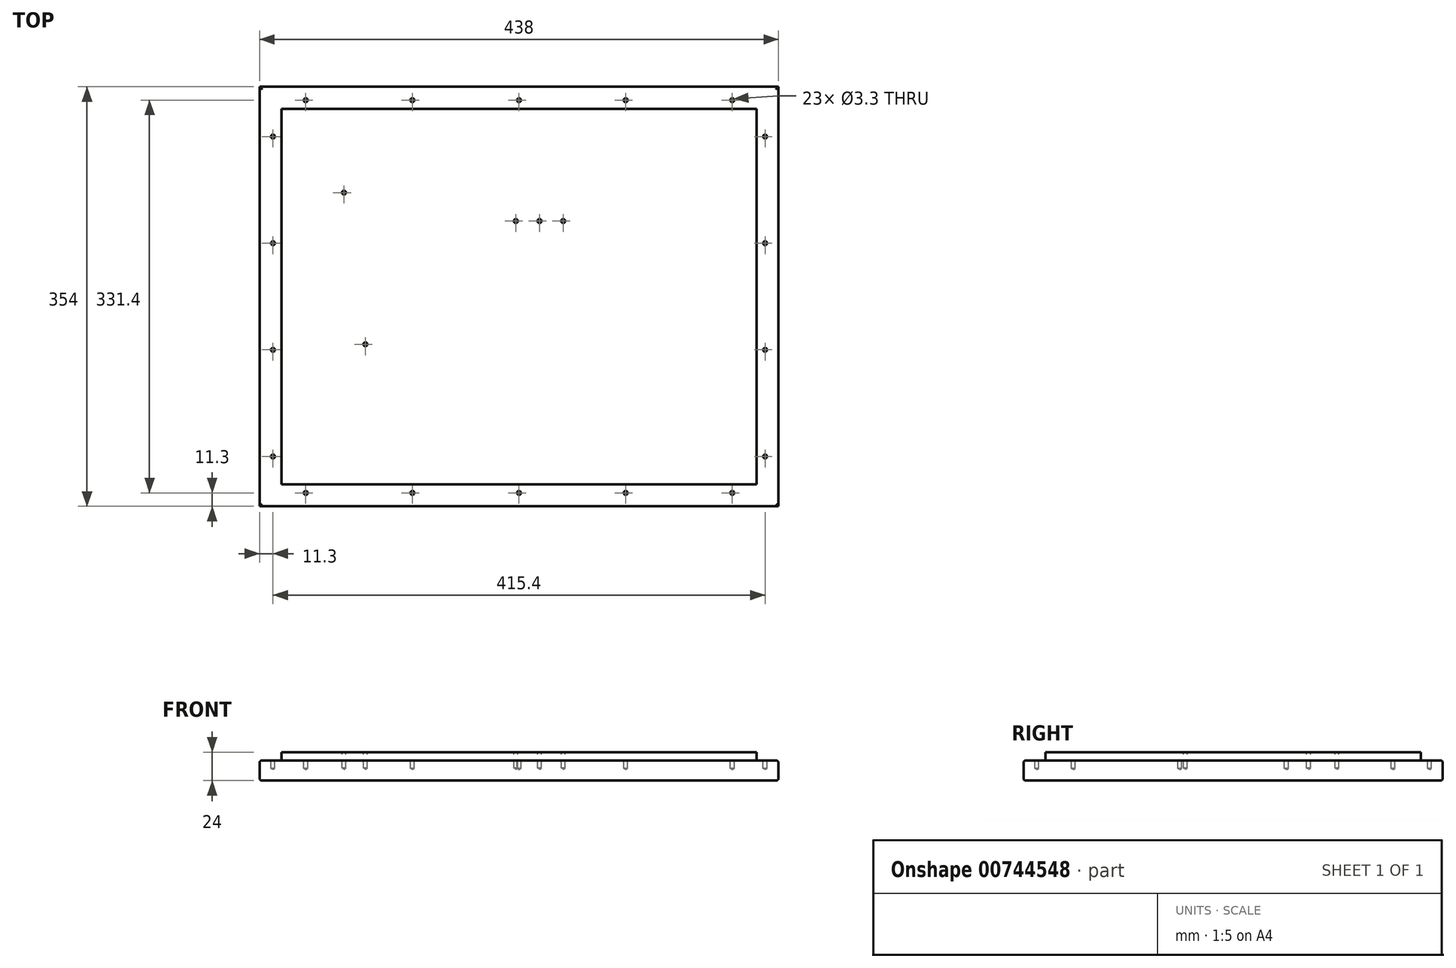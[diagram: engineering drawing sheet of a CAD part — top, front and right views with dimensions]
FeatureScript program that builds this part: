
annotation { "Feature Type Name" : "Feature", "Feature Type Description" : "" }
export const myFeature = defineFeature(function(context is Context, id is Id, definition is map)
    precondition{}
    {
        {
            var Q0;
            Q0=qCreatedBy(makeId("Top.planeOp"),FACE);
            var sketch = newSketch(context, id + "F0", { "sketchPlane" : qUnion([Q0])});
            skLineSegment(sketch, "E0.bottom", {"start": v(0, 0) * mm, "end": v(438, 0) * mm});
            skLineSegment(sketch, "E0.top", {"start": v(0, 354) * mm, "end": v(438, 354) * mm});
            skLineSegment(sketch, "E0.left", {"start": v(0, 0) * mm, "end": v(0, 354) * mm});
            skLineSegment(sketch, "E0.right", {"start": v(438, 0) * mm, "end": v(438, 354) * mm});
            skLineSegment(sketch, "E1.bottom", {"start": v(18.5, 18.5) * mm, "end": v(419.5, 18.5) * mm});
            skLineSegment(sketch, "E1.top", {"start": v(18.5, 335.5) * mm, "end": v(419.5, 335.5) * mm});
            skLineSegment(sketch, "E1.left", {"start": v(18.5, 18.5) * mm, "end": v(18.5, 335.5) * mm});
            skLineSegment(sketch, "E1.right", {"start": v(419.5, 18.5) * mm, "end": v(419.5, 335.5) * mm});
            skSolve(sketch);
        }
        {
            var Q0;
            Q0 = qSketchRegion(id + "F0", true);
            extrude(context, id + "F1", {"entities" : qUnion([Q0]), "depth" : 17 * mm, "offsetDistance" : 25 * mm});
        }
        {
            var Q0;
            Q0=makeQuery(id+"F0.imprint","IMPRINT",FACE,{"disambiguationData":[TD([[makeQuery(id+"F0.imprint","IMPRINT",EDGE,{"derivedFrom":sQuery(id+"F0.wireOp",EDGE,"E1.bottom")}),1.0]])]});
            extrude(context, id + "F2", {"entities" : qUnion([Q0]), "operationType" : NewBodyOperationType.ADD, "depth" : 24 * mm, "offsetDistance" : 25 * mm});
        }
        {
            var Q0;
            {var subQ0=sQuery(id+"F0.wireOp",EDGE,"E1.right");var subQ1=sQuery(id+"F0.wireOp",EDGE,"E1.left");var subQ2=sQuery(id+"F0.wireOp",EDGE,"E1.top");var subQ3=sQuery(id+"F0.wireOp",EDGE,"E1.bottom");Q0=makeQuery(id+"F2.boolean.opBoolean","MERGE",FACE,{"derivedFrom":[makeQuery(id+"F1.opExtrude","CAP_FACE",FACE,{"disambiguationData":[OSD([sQuery(id+"F0.wireOp",EDGE,"E0.bottom"),sQuery(id+"F0.wireOp",EDGE,"E0.top"),sQuery(id+"F0.wireOp",EDGE,"E0.left"),sQuery(id+"F0.wireOp",EDGE,"E0.right"),subQ3,subQ2,subQ1,subQ0])],"isStart":true}),makeQuery(id+"F2.opExtrude","CAP_FACE",FACE,{"disambiguationData":[OSD([subQ3,subQ2,subQ1,subQ0])],"isStart":true})]});}
            fillet(context, id + "F3", {"entities" : qUnion([Q0]), "radius" : 2 * mm, "tangentPropagation" : true, "allowEdgeOverflow" : false});
        }
        {
            var Q0;
            Q0=makeQuery(id+"F1.opExtrude","CAP_EDGE",EDGE,{"disambiguationData":[OSD([sQuery(id+"F0.wireOp",EDGE,"E0.right")])],"isStart":false});
            var Q1;
            Q1=makeQuery(id+"F1.opExtrude","CAP_EDGE",EDGE,{"disambiguationData":[OSD([sQuery(id+"F0.wireOp",EDGE,"E0.bottom")])],"isStart":false});
            var Q2;
            Q2=makeQuery(id+"F1.opExtrude","CAP_EDGE",EDGE,{"disambiguationData":[OSD([sQuery(id+"F0.wireOp",EDGE,"E0.top")])],"isStart":false});
            var Q3;
            Q3=makeQuery(id+"F1.opExtrude","CAP_EDGE",EDGE,{"disambiguationData":[OSD([sQuery(id+"F0.wireOp",EDGE,"E0.left")])],"isStart":false});
            fillet(context, id + "F4", {"entities" : qUnion([Q0, Q1, Q2, Q3]), "radius" : 2 * mm, "tangentPropagation" : true, "allowEdgeOverflow" : false});
        }
        {
            var Q0;
            Q0=makeQuery(id+"F1.opExtrude","CAP_FACE",FACE,{"disambiguationData":[OSD([sQuery(id+"F0.wireOp",EDGE,"E0.bottom"),sQuery(id+"F0.wireOp",EDGE,"E0.top"),sQuery(id+"F0.wireOp",EDGE,"E0.left"),sQuery(id+"F0.wireOp",EDGE,"E0.right"),sQuery(id+"F0.wireOp",EDGE,"E1.bottom"),sQuery(id+"F0.wireOp",EDGE,"E1.top"),sQuery(id+"F0.wireOp",EDGE,"E1.left"),sQuery(id+"F0.wireOp",EDGE,"E1.right")])],"isStart":false});
            var sketch = newSketch(context, id + "F5", { "sketchPlane" : qUnion([Q0])});
            skLineSegment(sketch, "E2", {"start": v(-30.1, 0) * mm, "end": v(521.52, 0) * mm, "construction": true});
            skLineSegment(sketch, "E3", {"start": v(-30.1, 42) * mm, "end": v(521.52, 42) * mm, "construction": true});
            skLineSegment(sketch, "E4", {"start": v(-30.1, 132) * mm, "end": v(521.52, 132) * mm, "construction": true});
            skLineSegment(sketch, "E5", {"start": v(-30.1, 222) * mm, "end": v(521.52, 222) * mm, "construction": true});
            skLineSegment(sketch, "E6", {"start": v(-30.1, 312) * mm, "end": v(521.52, 312) * mm, "construction": true});
            skLineSegment(sketch, "E7", {"start": v(0, -86.71) * mm, "end": v(0, 453.17) * mm, "construction": true});
            skLineSegment(sketch, "E8", {"start": v(11.3, -86.71) * mm, "end": v(11.3, 453.17) * mm, "construction": true});
            skLineSegment(sketch, "E9", {"start": v(426.7, -86.71) * mm, "end": v(426.7, 453.17) * mm, "construction": true});
            skLineSegment(sketch, "E10", {"start": v(0, 11.3) * mm, "end": v(551.61, 11.3) * mm, "construction": true});
            skLineSegment(sketch, "E11", {"start": v(0, 342.7) * mm, "end": v(482.91, 342.7) * mm, "construction": true});
            skLineSegment(sketch, "E12", {"start": v(39, -170.33) * mm, "end": v(39, 686.71) * mm, "construction": true});
            skLineSegment(sketch, "E13", {"start": v(129, -173.4) * mm, "end": v(129, 659.37) * mm, "construction": true});
            skLineSegment(sketch, "E14", {"start": v(219, -168.8) * mm, "end": v(219, 663.2) * mm, "construction": true});
            skLineSegment(sketch, "E15", {"start": v(309, -131.93) * mm, "end": v(309, 662.44) * mm, "construction": true});
            skLineSegment(sketch, "E16", {"start": v(399, -90.46) * mm, "end": v(399, 665.5) * mm, "construction": true});
            skPoint(sketch, "E17", {"position": v(219, 18.5) * mm});
            skCircle(sketch, "E18", {"center": v(11.3, 312) * mm, "radius": 2 * mm});
            skCircle(sketch, "E19", {"center": v(11.3, 222) * mm, "radius": 2 * mm});
            skCircle(sketch, "E20", {"center": v(11.3, 132) * mm, "radius": 2 * mm});
            skCircle(sketch, "E21", {"center": v(11.3, 42) * mm, "radius": 2 * mm});
            skCircle(sketch, "E22", {"center": v(426.7, 312) * mm, "radius": 2 * mm});
            skCircle(sketch, "E23", {"center": v(426.7, 222) * mm, "radius": 2 * mm});
            skCircle(sketch, "E24", {"center": v(426.7, 132) * mm, "radius": 2 * mm});
            skCircle(sketch, "E25", {"center": v(426.7, 42) * mm, "radius": 2 * mm});
            skCircle(sketch, "E26", {"center": v(39, 11.3) * mm, "radius": 2 * mm});
            skCircle(sketch, "E27", {"center": v(129, 11.3) * mm, "radius": 2 * mm});
            skCircle(sketch, "E28", {"center": v(219, 11.3) * mm, "radius": 2 * mm});
            skCircle(sketch, "E29", {"center": v(309, 11.3) * mm, "radius": 2 * mm});
            skCircle(sketch, "E30", {"center": v(399, 11.3) * mm, "radius": 2 * mm});
            skCircle(sketch, "E31", {"center": v(399, 342.7) * mm, "radius": 2 * mm});
            skCircle(sketch, "E32", {"center": v(309, 342.7) * mm, "radius": 2 * mm});
            skCircle(sketch, "E33", {"center": v(219, 342.7) * mm, "radius": 2 * mm});
            skCircle(sketch, "E34", {"center": v(129, 342.7) * mm, "radius": 2 * mm});
            skCircle(sketch, "E35", {"center": v(39, 342.7) * mm, "radius": 2 * mm});
            skSolve(sketch);
        }
        {
            var Q0;
            Q0=sQuery(id+"F5.wireOp",VERTEX,"E18.center");
            var Q1;
            Q1=sQuery(id+"F5.wireOp",VERTEX,"E19.center");
            var Q2;
            Q2=sQuery(id+"F5.wireOp",VERTEX,"E20.center");
            var Q3;
            Q3=sQuery(id+"F5.wireOp",VERTEX,"E21.center");
            var Q4;
            Q4=sQuery(id+"F5.wireOp",VERTEX,"E26.center");
            var Q5;
            Q5=sQuery(id+"F5.wireOp",VERTEX,"E27.center");
            var Q6;
            Q6=sQuery(id+"F5.wireOp",VERTEX,"E28.center");
            var Q7;
            Q7=sQuery(id+"F5.wireOp",VERTEX,"E29.center");
            var Q8;
            Q8=sQuery(id+"F5.wireOp",VERTEX,"E30.center");
            var Q9;
            Q9=sQuery(id+"F5.wireOp",VERTEX,"E25.center");
            var Q10;
            Q10=sQuery(id+"F5.wireOp",VERTEX,"E24.center");
            var Q11;
            Q11=sQuery(id+"F5.wireOp",VERTEX,"E23.center");
            var Q12;
            Q12=sQuery(id+"F5.wireOp",VERTEX,"E22.center");
            var Q13;
            Q13=sQuery(id+"F5.wireOp",VERTEX,"E31.center");
            var Q14;
            Q14=sQuery(id+"F5.wireOp",VERTEX,"E32.center");
            var Q15;
            Q15=sQuery(id+"F5.wireOp",VERTEX,"E33.center");
            var Q16;
            Q16=sQuery(id+"F5.wireOp",VERTEX,"E34.center");
            var Q17;
            Q17=sQuery(id+"F5.wireOp",VERTEX,"E35.center");
            var Q18;
            Q18=makeQuery(id+"F1.opExtrude","SWEPT_BODY",BODY,{"disambiguationData":[OSD([sQuery(id+"F0.wireOp",EDGE,"E0.bottom"),sQuery(id+"F0.wireOp",EDGE,"E0.top"),sQuery(id+"F0.wireOp",EDGE,"E0.left"),sQuery(id+"F0.wireOp",EDGE,"E0.right"),sQuery(id+"F0.wireOp",EDGE,"E1.bottom"),sQuery(id+"F0.wireOp",EDGE,"E1.top"),sQuery(id+"F0.wireOp",EDGE,"E1.left"),sQuery(id+"F0.wireOp",EDGE,"E1.right")])]});
            hole(context, id + "F6", {"style" : HoleStyle.SIMPLE, "endStyle" : HoleEndStyle.BLIND, "standardTappedOrClearance" : lookupTablePath({ "standard" : "ISO", "engagement" : "75%", "pitch" : "0.7 mm", "size" : "M4", "type" : "Tapped" }), "standardBlindInLast" : lookupTablePath({ "standard" : "ISO", "engagement" : "75%", "pitch" : "0.7 mm", "size" : "M4", "type" : "Tapped" }), "holeDiameter" : 3.3 * mm, "majorDiameter" : 4 * mm, "showTappedDepth" : true, "holeDepth" : 6.6 * mm, "isTappedThrough" : true, "tappedDepth" : 5.9 * mm, "tapClearance" : 1, "locations" : qUnion([Q0, Q1, Q2, Q3, Q4, Q5, Q6, Q7, Q8, Q9, Q10, Q11, Q12, Q13, Q14, Q15, Q16, Q17]), "scope" : qUnion([Q18])});
        }
        {
            var Q0;
            Q0=makeQuery(id+"F2.opExtrude","CAP_FACE",FACE,{"disambiguationData":[OSD([sQuery(id+"F0.wireOp",EDGE,"E1.bottom"),sQuery(id+"F0.wireOp",EDGE,"E1.top"),sQuery(id+"F0.wireOp",EDGE,"E1.left"),sQuery(id+"F0.wireOp",EDGE,"E1.right")])],"isStart":false});
            var sketch = newSketch(context, id + "F7", { "sketchPlane" : qUnion([Q0])});
            skCircle(sketch, "E36", {"center": v(216.3, 240.7) * mm, "radius": 1.5 * mm});
            skCircle(sketch, "E37.0", {"center": v(11.3, 222) * mm, "radius": 1.65 * mm});
            skCircle(sketch, "E38.0", {"center": v(219, 342.7) * mm, "radius": 1.65 * mm});
            skCircle(sketch, "E39.0", {"center": v(11.3, 312) * mm, "radius": 1.65 * mm});
            skCircle(sketch, "E40.0", {"center": v(39, 342.7) * mm, "radius": 1.65 * mm});
            skCircle(sketch, "E41.1.0.0", {"center": v(236.3, 240.7) * mm, "radius": 1.5 * mm});
            skCircle(sketch, "E41.2.0.0", {"center": v(256.3, 240.7) * mm, "radius": 1.5 * mm});
            skLineSegment(sketch, "E41.direction1", {"start": v(216.3, 240.7) * mm, "end": v(236.3, 240.7) * mm, "construction": true});
            skCircle(sketch, "E42", {"center": v(71.3, 264.7) * mm, "radius": 1.5 * mm});
            skCircle(sketch, "E43", {"center": v(89.3, 136.7) * mm, "radius": 1.5 * mm});
            skLineSegment(sketch, "E44", {"start": v(104.3, 335.5) * mm, "end": v(104.3, 18.5) * mm, "construction": true});
            skSolve(sketch);
        }
        {
            var Q0;
            Q0=sQuery(id+"F7.wireOp",VERTEX,"E41.direction1.start");
            var Q1;
            Q1=sQuery(id+"F7.wireOp",VERTEX,"E41.direction1.end");
            var Q2;
            Q2=sQuery(id+"F7.wireOp",VERTEX,"E41.2.0.0.center");
            var Q3;
            Q3=makeQuery(id+"F1.opExtrude","SWEPT_BODY",BODY,{"disambiguationData":[OSD([sQuery(id+"F0.wireOp",EDGE,"E0.bottom"),sQuery(id+"F0.wireOp",EDGE,"E0.top"),sQuery(id+"F0.wireOp",EDGE,"E0.left"),sQuery(id+"F0.wireOp",EDGE,"E0.right"),sQuery(id+"F0.wireOp",EDGE,"E1.bottom"),sQuery(id+"F0.wireOp",EDGE,"E1.top"),sQuery(id+"F0.wireOp",EDGE,"E1.left"),sQuery(id+"F0.wireOp",EDGE,"E1.right")])]});
            hole(context, id + "F8", {"style" : HoleStyle.SIMPLE, "endStyle" : HoleEndStyle.BLIND, "standardTappedOrClearance" : lookupTablePath({ "fit" : "Normal", "standard" : "ISO", "size" : "M3", "type" : "Clearance" }), "standardBlindInLast" : lookupTablePath({ "fit" : "Standard", "standard" : "ISO", "size" : "M3", "type" : "Clearance" }), "holeDiameter" : 3.3 * mm, "majorDiameter" : 3 * mm, "holeDepth" : 13.5 * mm, "isTappedThrough" : true, "tappedDepth" : 12 * mm, "tapClearance" : 3, "locations" : qUnion([Q0, Q1, Q2]), "scope" : qUnion([Q3])});
        }
        {
            var Q0;
            Q0=sQuery(id+"F7.wireOp",VERTEX,"E42.center");
            var Q1;
            Q1=sQuery(id+"F7.wireOp",VERTEX,"E43.center");
            var Q2;
            Q2=makeQuery(id+"F1.opExtrude","SWEPT_BODY",BODY,{"disambiguationData":[OSD([sQuery(id+"F0.wireOp",EDGE,"E0.bottom"),sQuery(id+"F0.wireOp",EDGE,"E0.top"),sQuery(id+"F0.wireOp",EDGE,"E0.left"),sQuery(id+"F0.wireOp",EDGE,"E0.right"),sQuery(id+"F0.wireOp",EDGE,"E1.bottom"),sQuery(id+"F0.wireOp",EDGE,"E1.top"),sQuery(id+"F0.wireOp",EDGE,"E1.left"),sQuery(id+"F0.wireOp",EDGE,"E1.right")])]});
            hole(context, id + "F9", {"style" : HoleStyle.SIMPLE, "endStyle" : HoleEndStyle.BLIND, "standardTappedOrClearance" : lookupTablePath({ "fit" : "Normal", "standard" : "ISO", "size" : "M3", "type" : "Clearance" }), "standardBlindInLast" : lookupTablePath({ "fit" : "Standard", "standard" : "ISO", "size" : "M3", "type" : "Clearance" }), "holeDiameter" : 3.3 * mm, "majorDiameter" : 5 * mm, "holeDepth" : 13.5 * mm, "isTappedThrough" : true, "tappedDepth" : 12 * mm, "tapClearance" : 3, "locations" : qUnion([Q0, Q1]), "scope" : qUnion([Q2])});
        }
    });
